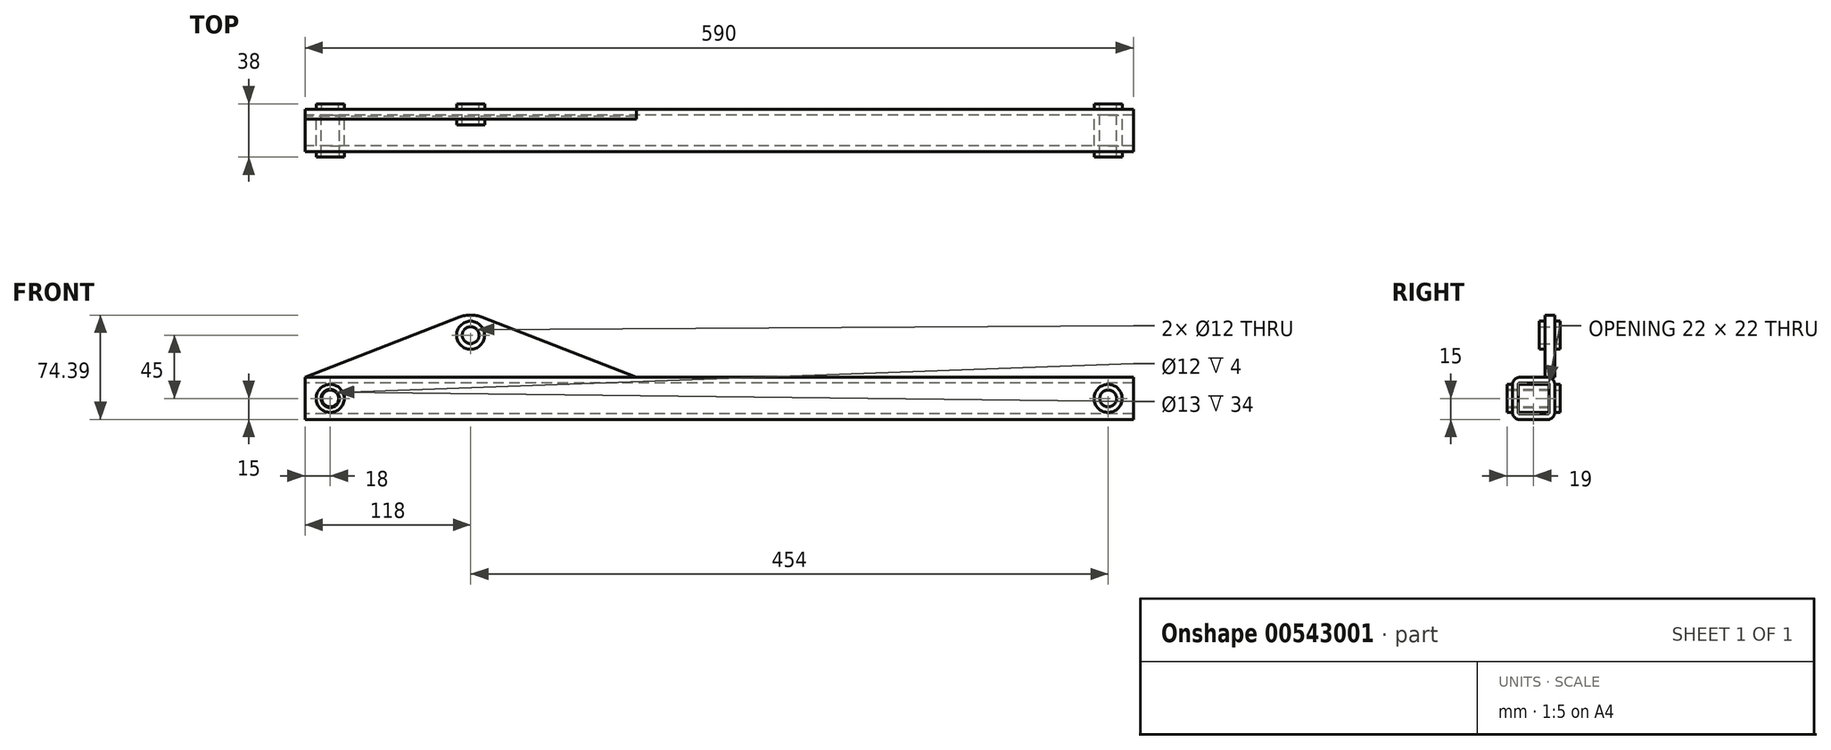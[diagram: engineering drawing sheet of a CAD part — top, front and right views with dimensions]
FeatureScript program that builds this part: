
annotation { "Feature Type Name" : "Feature", "Feature Type Description" : "" }
export const myFeature = defineFeature(function(context is Context, id is Id, definition is map)
    precondition{}
    {
        {
            var Q0;
            Q0=qCreatedBy(makeId("Right.planeOp"),FACE);
            var sketch = newSketch(context, id + "F0", { "sketchPlane" : qUnion([Q0])});
            skLineSegment(sketch, "E0", {"start": v(0, 5) * mm, "end": v(0, 25) * mm});
            skLineSegment(sketch, "E1", {"start": v(-5, 30) * mm, "end": v(-25, 30) * mm});
            skLineSegment(sketch, "E2", {"start": v(-30, 25) * mm, "end": v(-30, 5) * mm});
            skLineSegment(sketch, "E3", {"start": v(-25, 0) * mm, "end": v(-5, 0) * mm});
            skPoint(sketch, "E4.visualSharp", {"position": v(-30, 30) * mm});
            skArc(sketch, "E4.filletArc", {"start": v(-25, 30) * mm, "mid": v(-28.54, 28.54) * mm, "end": v(-30, 25) * mm});
            skPoint(sketch, "E5.visualSharp", {"position": v(0, 30) * mm});
            skArc(sketch, "E5.filletArc", {"start": v(0, 25) * mm, "mid": v(-1.46, 28.54) * mm, "end": v(-5, 30) * mm});
            skPoint(sketch, "E6.visualSharp", {"position": v(-30, 0) * mm});
            skArc(sketch, "E6.filletArc", {"start": v(-30, 5) * mm, "mid": v(-28.54, 1.46) * mm, "end": v(-25, 0) * mm});
            skPoint(sketch, "E7.visualSharp", {"position": v(0, 0) * mm});
            skArc(sketch, "E7.filletArc", {"start": v(-5, 0) * mm, "mid": v(-1.46, 1.46) * mm, "end": v(0, 5) * mm});
            skArc(sketch, "E8.0", {"start": v(-25, 26) * mm, "mid": v(-25.7, 25.7) * mm, "end": v(-26, 25) * mm});
            skLineSegment(sketch, "E8.1", {"start": v(-5, 26) * mm, "end": v(-25, 26) * mm});
            skLineSegment(sketch, "E8.2", {"start": v(-26, 25) * mm, "end": v(-26, 5) * mm});
            skArc(sketch, "E8.3", {"start": v(-4, 25) * mm, "mid": v(-4.3, 25.7) * mm, "end": v(-5, 26) * mm});
            skArc(sketch, "E8.4", {"start": v(-26, 5) * mm, "mid": v(-25.7, 4.3) * mm, "end": v(-25, 4) * mm});
            skLineSegment(sketch, "E8.5", {"start": v(-25, 4) * mm, "end": v(-5, 4) * mm});
            skArc(sketch, "E8.6", {"start": v(-5, 4) * mm, "mid": v(-4.3, 4.3) * mm, "end": v(-4, 5) * mm});
            skLineSegment(sketch, "E8.7", {"start": v(-4, 5) * mm, "end": v(-4, 25) * mm});
            skSolve(sketch);
        }
        {
            var Q0;
            Q0=makeQuery(id+"F0.imprint","IMPRINT",FACE,{"disambiguationData":[TD([[makeQuery(id+"F0.imprint","IMPRINT",EDGE,{"derivedFrom":sQuery(id+"F0.wireOp",EDGE,"E0")}),1.0]])]});
            extrude(context, id + "F1", {"entities" : qUnion([Q0]), "flatOperationType" : FlatOperationType.REMOVE, "depth" : 590 * mm, "offsetDistance" : 25 * mm, "domain" : OperationDomain.MODEL});
        }
        {
            var Q0;
            Q0=qCreatedBy(makeId("Front.planeOp"),FACE);
            var sketch = newSketch(context, id + "F2", { "sketchPlane" : qUnion([Q0])});
            skLineSegment(sketch, "E9.0", {"start": v(0, 5) * mm, "end": v(0, 25) * mm, "construction": true});
            skLineSegment(sketch, "E10", {"start": v(0, 15) * mm, "end": v(18, 15) * mm, "construction": true});
            skPoint(sketch, "E10.endSnap0", {"position": v(0, 15) * mm});
            skCircle(sketch, "E11", {"center": v(18, 15) * mm, "radius": 6 * mm});
            skCircle(sketch, "E12.0", {"center": v(18, 15) * mm, "radius": 10 * mm});
            skLineSegment(sketch, "E13.0", {"start": v(590, 5) * mm, "end": v(590, 25) * mm});
            skLineSegment(sketch, "E14", {"start": v(590, 15) * mm, "end": v(572, 15) * mm, "construction": true});
            skCircle(sketch, "E15", {"center": v(572, 15) * mm, "radius": 6 * mm});
            skCircle(sketch, "E16.0", {"center": v(572, 15) * mm, "radius": 10 * mm});
            skCircle(sketch, "E17.0", {"center": v(18, 15) * mm, "radius": 6.5 * mm});
            skLineSegment(sketch, "E18", {"start": v(18, 15) * mm, "end": v(118, 15) * mm, "construction": true});
            skLineSegment(sketch, "E19", {"start": v(0, 30) * mm, "end": v(110, 72.89) * mm});
            skLineSegment(sketch, "E20", {"start": v(118, 15) * mm, "end": v(236, 15) * mm, "construction": true});
            skLineSegment(sketch, "E21", {"start": v(236, 15) * mm, "end": v(236, 36.4) * mm, "construction": true});
            skLineSegment(sketch, "E22", {"start": v(126, 72.89) * mm, "end": v(236, 30) * mm});
            skLineSegment(sketch, "E23", {"start": v(236, 30) * mm, "end": v(0, 30) * mm});
            skCircle(sketch, "E24", {"center": v(118, 60) * mm, "radius": 6 * mm});
            skCircle(sketch, "E25.0", {"center": v(118, 60) * mm, "radius": 10 * mm});
            skLineSegment(sketch, "E26", {"start": v(118, 15) * mm, "end": v(118, 60) * mm, "construction": true});
            skLineSegment(sketch, "E27", {"start": v(118, 76) * mm, "end": v(118, 60) * mm, "construction": true});
            skPoint(sketch, "E28.visualSharp", {"position": v(118, 76) * mm});
            skArc(sketch, "E28.filletArc", {"start": v(126, 72.89) * mm, "mid": v(118, 74.39) * mm, "end": v(110, 72.89) * mm});
            skSolve(sketch);
        }
        {
            var Q0;
            Q0=makeQuery(id+"F2.imprint","IMPRINT",FACE,{"disambiguationData":[TD([[makeQuery(id+"F2.imprint","IMPRINT",EDGE,{"derivedFrom":sQuery(id+"F2.wireOp",EDGE,"E15")}),1.0]])]});
            var Q1;
            Q1=makeQuery(id+"F2.imprint","IMPRINT",FACE,{"disambiguationData":[TD([[makeQuery(id+"F2.imprint","IMPRINT",EDGE,{"derivedFrom":sQuery(id+"F2.wireOp",EDGE,"E11")}),1.0]])]});
            extrude(context, id + "F3", {"entities" : qUnion([Q0, Q1]), "operationType" : NewBodyOperationType.REMOVE, "endBound" : BoundingType.THROUGH_ALL, "depth" : 38.9 * mm, "offsetDistance" : 25 * mm});
        }
        {
            var Q0;
            Q0=makeQuery(id+"F2.imprint","IMPRINT",FACE,{"disambiguationData":[TD([[makeQuery(id+"F2.imprint","IMPRINT",EDGE,{"derivedFrom":sQuery(id+"F2.wireOp",EDGE,"E15")}),-1.0]])]});
            var Q1;
            Q1=makeQuery(id+"F2.imprint","IMPRINT",FACE,{"disambiguationData":[TD([[makeQuery(id+"F2.imprint","IMPRINT",EDGE,{"derivedFrom":sQuery(id+"F2.wireOp",EDGE,"E11")}),-1.0]])]});
            extrude(context, id + "F4", {"entities" : qUnion([Q0, Q1]), "operationType" : NewBodyOperationType.ADD, "depth" : 34 * mm, "offsetDistance" : 25 * mm});
        }
        {
            var Q0;
            Q0=makeQuery(id+"F2.imprint","IMPRINT",FACE,{"disambiguationData":[TD([[makeQuery(id+"F2.imprint","IMPRINT",EDGE,{"derivedFrom":sQuery(id+"F2.wireOp",EDGE,"E15")}),-1.0]])]});
            var Q1;
            Q1=makeQuery(id+"F2.imprint","IMPRINT",FACE,{"disambiguationData":[TD([[makeQuery(id+"F2.imprint","IMPRINT",EDGE,{"derivedFrom":sQuery(id+"F2.wireOp",EDGE,"E11")}),-1.0]])]});
            extrude(context, id + "F5", {"entities" : qUnion([Q0, Q1]), "operationType" : NewBodyOperationType.ADD, "oppositeDirection" : true, "depth" : 4 * mm, "offsetDistance" : 25 * mm});
        }
        {
            var Q0;
            Q0=makeQuery(id+"F2.imprint","IMPRINT",FACE,{"disambiguationData":[TD([[makeQuery(id+"F2.imprint","IMPRINT",EDGE,{"derivedFrom":sQuery(id+"F2.wireOp",EDGE,"E19")}),-1.0]])]});
            extrude(context, id + "F6", {"entities" : qUnion([Q0]), "operationType" : NewBodyOperationType.ADD, "depth" : 7 * mm, "offsetDistance" : 25 * mm});
        }
        {
            var Q0;
            Q0=makeQuery(id+"F2.imprint","IMPRINT",FACE,{"disambiguationData":[TD([[makeQuery(id+"F2.imprint","IMPRINT",EDGE,{"derivedFrom":sQuery(id+"F2.wireOp",EDGE,"E24")}),-1.0]])]});
            extrude(context, id + "F7", {"entities" : qUnion([Q0]), "operationType" : NewBodyOperationType.ADD, "depth" : 11 * mm, "offsetDistance" : 25 * mm});
        }
        {
            var Q0;
            Q0=makeQuery(id+"F2.imprint","IMPRINT",FACE,{"disambiguationData":[TD([[makeQuery(id+"F2.imprint","IMPRINT",EDGE,{"derivedFrom":sQuery(id+"F2.wireOp",EDGE,"E24")}),-1.0]])]});
            extrude(context, id + "F8", {"entities" : qUnion([Q0]), "operationType" : NewBodyOperationType.ADD, "oppositeDirection" : true, "depth" : 4 * mm, "offsetDistance" : 25 * mm});
        }
        {
            var Q0;
            Q0=makeQuery(id+"F2.imprint","IMPRINT",FACE,{"disambiguationData":[TD([[makeQuery(id+"F2.imprint","IMPRINT",EDGE,{"derivedFrom":sQuery(id+"F2.wireOp",EDGE,"E17.0")}),1.0]])]});
            extrude(context, id + "F9", {"entities" : qUnion([Q0]), "operationType" : NewBodyOperationType.REMOVE, "endBound" : BoundingType.THROUGH_ALL, "depth" : 15.3 * mm, "offsetDistance" : 25 * mm});
        }
        {
            var Q0;
            Q0=makeQuery(id+"F2.imprint","IMPRINT",FACE,{"disambiguationData":[TD([[makeQuery(id+"F2.imprint","IMPRINT",EDGE,{"derivedFrom":sQuery(id+"F2.wireOp",EDGE,"E12.0")}),1.0]])]});
            extrude(context, id + "F10", {"entities" : qUnion([Q0]), "operationType" : NewBodyOperationType.ADD, "depth" : 34 * mm, "offsetDistance" : 25 * mm});
        }
        {
            var Q0;
            Q0=makeQuery(id+"F2.imprint","IMPRINT",FACE,{"disambiguationData":[TD([[makeQuery(id+"F2.imprint","IMPRINT",EDGE,{"derivedFrom":sQuery(id+"F2.wireOp",EDGE,"E12.0")}),1.0]])]});
            extrude(context, id + "F11", {"entities" : qUnion([Q0]), "operationType" : NewBodyOperationType.ADD, "oppositeDirection" : true, "depth" : 4 * mm, "offsetDistance" : 25 * mm});
        }
    });
